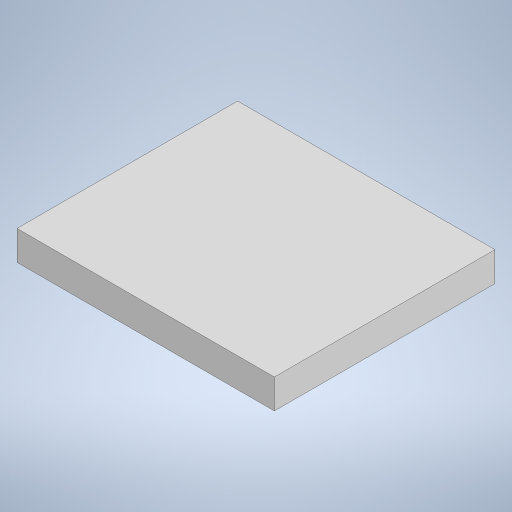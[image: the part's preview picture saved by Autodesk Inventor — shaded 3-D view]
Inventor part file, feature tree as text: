
AUTODESK INVENTOR PART (.ipt)
format: ipt  version: 2023 (Build 270158000, 158)  size: 193,024 bytes
history: native  units: mm
features: other x1, extrude x1, sketch x1
ambient origin geometry x8: Origin, YZ Plane, XZ Plane, XY Plane, X Axis, Y Axis, Z Axis, Center Point
bodies: Body1 (feature_tree)
feature tree (3):
  other  "Bryła1"
  extrude  "Wyciągnięcie proste1"  Depth=35.0mm
  sketch  "Szkic1"
